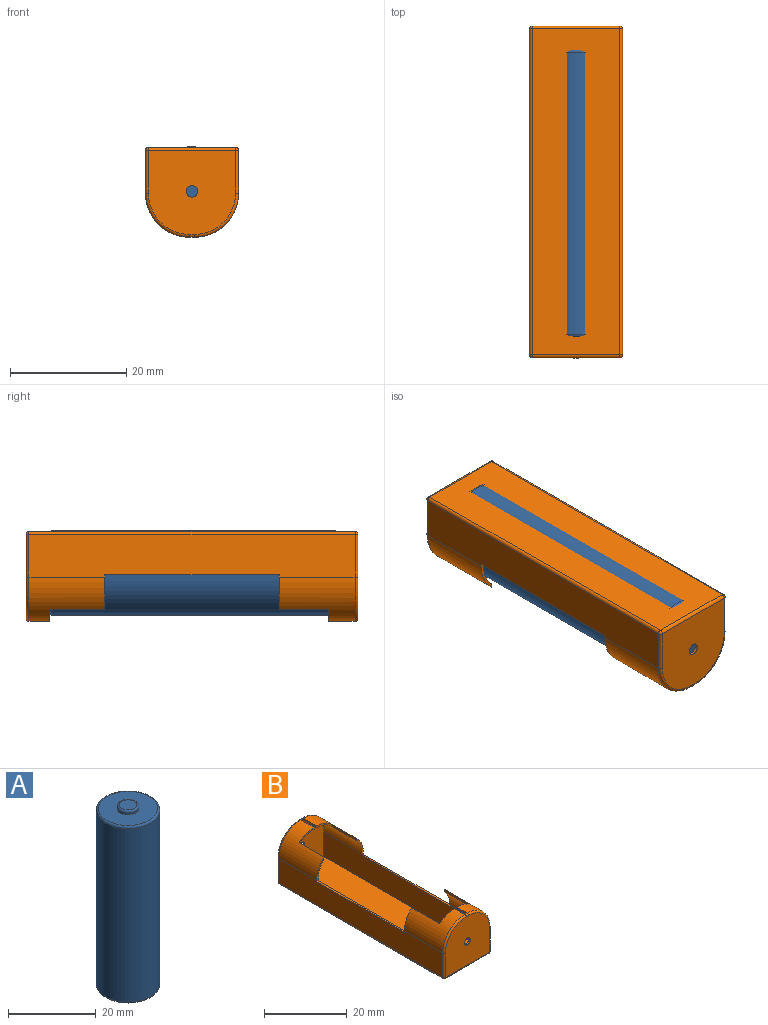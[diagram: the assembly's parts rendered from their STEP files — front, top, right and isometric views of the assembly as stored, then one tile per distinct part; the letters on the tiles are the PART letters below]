
ASSEMBLY  parts=2 mates=1
PART A: 8 faces, bbox 15.7x15.7x50.5 mm
  f0: cylinder r=7.25mm len=48.5mm, axis (0,0,-1), area 2209.3mm2, adj f6,f7
  f1: plane 13.5x13.5mm, normal (0,0,-1), area 143.1mm2, adj f7
  f2: cylinder r=2.5mm len=5mm, axis (0,0,1), area 7.9mm2, adj f3,f5
  f3: plane 13.5x13.5mm, normal (0,0,1), area 123.5mm2, adj f2,f6
  f4: plane 4x4mm, normal (0,0,1), area 12.6mm2, adj f5
  f5: torus R=2mm, axis (0,0,1), area 11.4mm2, adj f2,f4
  f6: torus R=6.75mm, axis (0,0,1), area 34.9mm2, adj f0,f3
  f7: torus R=6.75mm, axis (0,0,1), area 34.9mm2, adj f0,f1
PART B: 56 faces, bbox 17.3x57x16 mm
  f0: cylinder r=7.6mm len=13mm, axis (0,1,0), area 102.1mm2, adj f2,f6,f15,f19,f50,f51
  f1: cylinder r=7.6mm len=13mm, axis (0,-1,0), area 102.1mm2, adj f3,f17,f23,f45,f52,f53
  f2: plane 3.5x0.5mm, normal (1,0,0), area 1.8mm2, adj f0,f4,f39,f51
  f3: plane 3.5x0.5mm, normal (-1,0,0), area 1.8mm2, adj f1,f5,f39,f53
  f4: cylinder r=7.1mm len=13mm, axis (0,1,0), area 90.9mm2, adj f2,f6,f38,f39,f50,f51
  f5: cylinder r=7.1mm len=13mm, axis (0,-1,0), area 90.9mm2, adj f3,f39,f40,f45,f52,f53
  f6: plane 6.03x2.5mm, normal (0,1,0), area 3.2mm2, adj f0,f4,f15,f38,f47,f50
  f7: plane 6.03x2.5mm, normal (0,-1,0), area 3.2mm2, adj f8,f12,f15,f38,f47,f48
  f8: cylinder r=7.6mm len=13mm, axis (0,1,0), area 107.7mm2, adj f7,f10,f15,f28,f48,f49
  f9: cylinder r=7.6mm len=13mm, axis (0,-1,0), area 107.7mm2, adj f11,f17,f34,f44,f54,f55
  f10: plane 4.5x0.5mm, normal (1,0,0), area 2.3mm2, adj f8,f12,f37,f49
  f11: plane 4.5x0.5mm, normal (-1,0,0), area 2.3mm2, adj f9,f13,f37,f55
  f12: cylinder r=7.1mm len=13mm, axis (0,1,0), area 96.6mm2, adj f7,f10,f37,f38,f48,f49
  f13: cylinder r=7.1mm len=13mm, axis (0,-1,0), area 96.6mm2, adj f11,f37,f40,f44,f54,f55
  f14: plane 15x14.4mm, normal (0,1,0), area 191.2mm2, adj f24,f28,f31,f32,f34,f36,f43
  f15: plane 56x7.3mm, normal (-1,0,0), area 396.8mm2, adj f0,f6,f7,f8,f20,f24,f25,f47
  f16: plane 15x14.4mm, normal (0,-1,0), area 191.2mm2, adj f19,f20,f21,f23,f26,f27,f42
  f17: plane 56x7.3mm, normal (1,0,0), area 396.8mm2, adj f1,f9,f27,f33,f36,f44,f45,f46
  f18: plane 56x15mm, normal (0,0,-1), area 840mm2, adj f25,f26,f32,f33
  f19: torus R=7.1mm, axis (0,1,0), area 9.2mm2, adj f0,f16,f20,f21
  f20: cylinder r=0.5mm len=7.3mm, axis (0,0,-1), area 5.7mm2, adj f15,f16,f19,f22
  f21: cylinder r=0.5mm len=0.8mm, axis (-1,0,0), area 0.6mm2, adj f16,f19,f23,f39
  f22: sphere r=0.5mm, area 0.4mm2, adj f20,f25,f26
  f23: torus R=7.1mm, axis (0,1,0), area 9.2mm2, adj f1,f16,f21,f27
  f24: cylinder r=0.5mm len=7.3mm, axis (0,0,1), area 5.7mm2, adj f14,f15,f28,f29
  f25: cylinder r=0.5mm len=56mm, axis (0,-1,0), area 44mm2, adj f15,f18,f22,f29
  f26: cylinder r=0.5mm len=15mm, axis (1,0,0), area 11.8mm2, adj f16,f18,f22,f30
  f27: cylinder r=0.5mm len=7.3mm, axis (0,0,1), area 5.7mm2, adj f16,f17,f23,f30
  f28: torus R=7.1mm, axis (0,1,0), area 9.2mm2, adj f8,f14,f24,f31
  f29: sphere r=0.5mm, area 0.4mm2, adj f24,f25,f32
  f30: sphere r=0.5mm, area 0.4mm2, adj f26,f27,f33
  f31: cylinder r=0.5mm len=0.8mm, axis (1,0,0), area 0.6mm2, adj f14,f28,f34,f37
  f32: cylinder r=0.5mm len=15mm, axis (-1,0,0), area 11.8mm2, adj f14,f18,f29,f35
  f33: cylinder r=0.5mm len=56mm, axis (0,1,0), area 44mm2, adj f17,f18,f30,f35
  f34: torus R=7.1mm, axis (0,1,0), area 9.2mm2, adj f9,f14,f31,f36
  f35: sphere r=0.5mm, area 0.4mm2, adj f32,f33,f36
  f36: cylinder r=0.5mm len=7.3mm, axis (0,0,-1), area 5.7mm2, adj f14,f17,f34,f35
  f37: plane 15x14.9mm, normal (0,-1,0), area 191.6mm2, adj f10,f11,f12,f13,f31,f38,f40,f41
  f38: plane 56x7.3mm, normal (1,0,0), area 396.8mm2, adj f4,f6,f7,f12,f37,f39,f41,f47
  f39: plane 15x14.9mm, normal (0,1,0), area 191.6mm2, adj f2,f3,f4,f5,f21,f38,f40,f41
  f40: plane 56x7.3mm, normal (-1,0,0), area 396.8mm2, adj f5,f13,f37,f39,f41,f44,f45,f46
  f41: plane 56x15mm, normal (0,0,1), area 840mm2, adj f37,f38,f39,f40
  f42: cylinder r=1mm len=2mm, axis (0,-1,0), area 3.1mm2, adj f16,f39
  f43: cylinder r=1mm len=2mm, axis (0,-1,0), area 3.1mm2, adj f14,f37
  f44: plane 6.03x2.5mm, normal (0,-1,0), area 3.2mm2, adj f9,f13,f17,f40,f46,f54
  f45: plane 6.03x2.5mm, normal (0,1,0), area 3.2mm2, adj f1,f5,f17,f40,f46,f52
  f46: plane 30x0.5mm, normal (0,0,1), area 15mm2, adj f17,f40,f44,f45
  f47: plane 30x0.5mm, normal (0,0,1), area 15mm2, adj f6,f7,f15,f38
  f48: plane 8.5x0.7mm, normal (1,0,0), area 5.9mm2, adj f7,f8,f12,f49
  f49: plane 5.1x2.66mm, normal (0,-1,0), area 2.8mm2, adj f8,f10,f12,f48
  f50: plane 9.5x0.7mm, normal (1,0,0), area 6.6mm2, adj f0,f4,f6,f51
  f51: plane 5.1x2.66mm, normal (0,1,0), area 2.8mm2, adj f0,f2,f4,f50
  f52: plane 9.5x0.7mm, normal (-1,0,0), area 6.6mm2, adj f1,f5,f45,f53
  f53: plane 5.1x2.66mm, normal (0,1,0), area 2.8mm2, adj f1,f3,f5,f52
  f54: plane 8.5x0.7mm, normal (-1,0,0), area 5.9mm2, adj f9,f13,f44,f55
  f55: plane 5.1x2.66mm, normal (0,-1,0), area 2.8mm2, adj f9,f11,f13,f54
PLACE A rot(axis=(1,0,0),90deg) t=(37.5,29.45,3.8)mm
PLACE B rot(axis=(1,0,0),180deg) t=(37.5,33.45,10.89)mm
MATE fastened B.f37 <-> A.f2  axis (0,1,0) through (37.5,-23.05,3.8)mm
